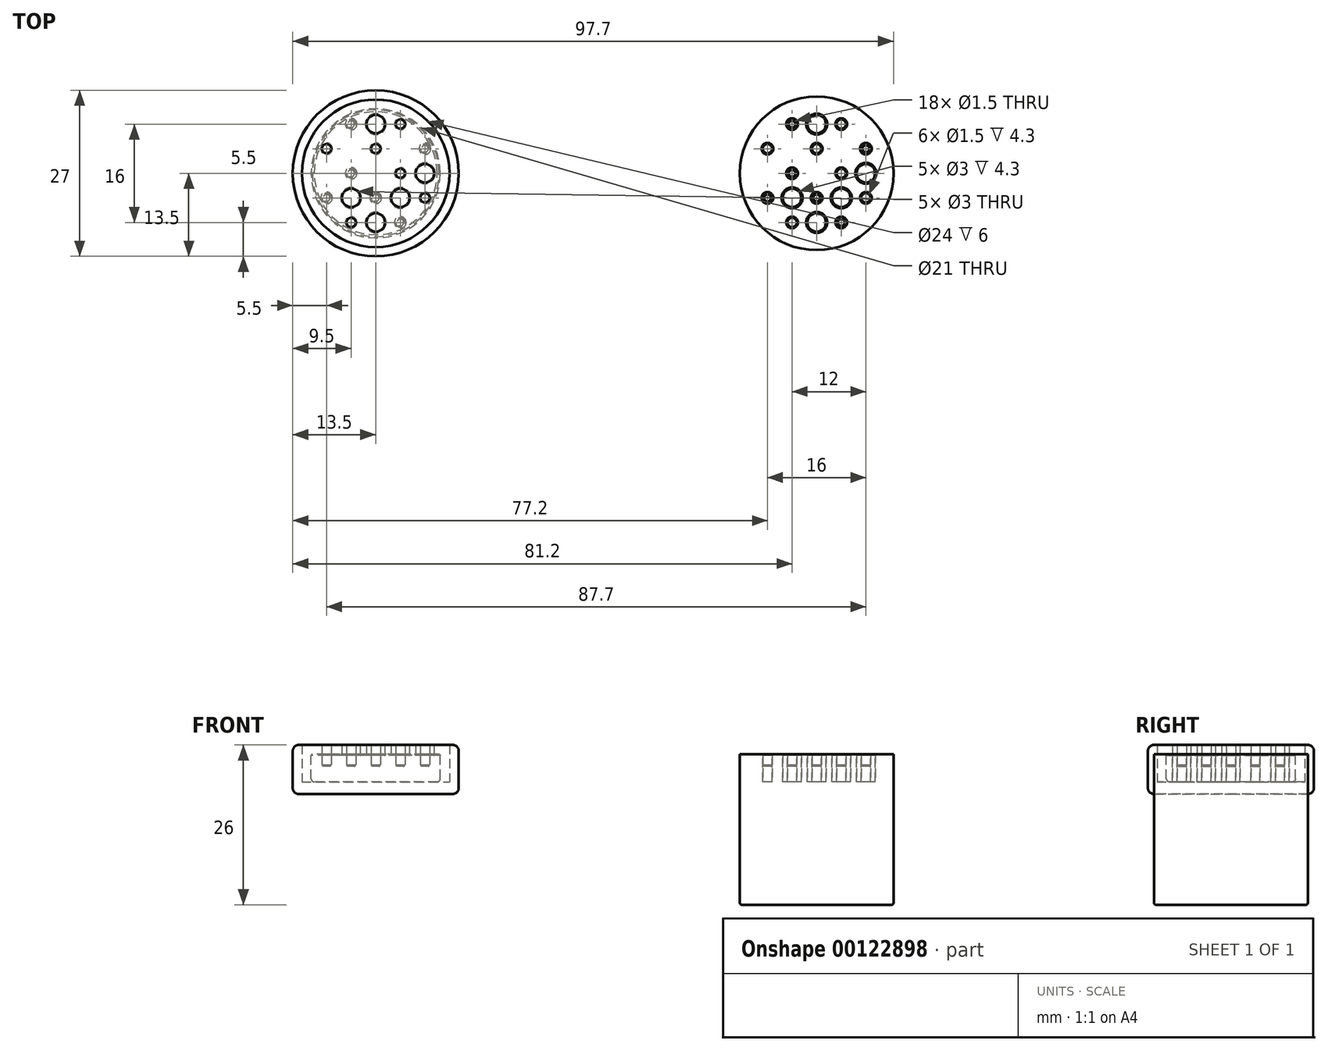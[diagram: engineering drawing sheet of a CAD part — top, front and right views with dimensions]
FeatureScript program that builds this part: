
annotation { "Feature Type Name" : "Feature", "Feature Type Description" : "" }
export const myFeature = defineFeature(function(context is Context, id is Id, definition is map)
    precondition{}
    {
        {
            var Q0;
            Q0=qCreatedBy(makeId("Top.planeOp"),FACE);
            var sketch = newSketch(context, id + "F0", { "sketchPlane" : qUnion([Q0])});
            skCircle(sketch, "E0", {"center": v(0, 0) * mm, "radius": 10.5 * mm});
            skCircle(sketch, "E1", {"center": v(0, 0) * mm, "radius": 1.5 * mm});
            skLineSegment(sketch, "E2", {"start": v(-10.5, 0) * mm, "end": v(10.5, 0) * mm, "construction": true});
            skCircle(sketch, "E3", {"center": v(-8, 0) * mm, "radius": 1.5 * mm});
            skLineSegment(sketch, "E4", {"start": v(0, 10.5) * mm, "end": v(0, -10.5) * mm, "construction": true});
            skCircle(sketch, "E5.MirrorC", {"center": v(8, 0) * mm, "radius": 1.5 * mm});
            skLineSegment(sketch, "E6", {"start": v(-7.42, 7.42) * mm, "end": v(7.42, -7.42) * mm, "construction": true});
            skCircle(sketch, "E7", {"center": v(-4, 4) * mm, "radius": 1.5 * mm});
            skLineSegment(sketch, "E8", {"start": v(-7.42, -7.42) * mm, "end": v(7.42, 7.42) * mm, "construction": true});
            skLineSegment(sketch, "E9", {"start": v(-10.25, -2.25) * mm, "end": v(2.25, 10.25) * mm, "construction": true});
            skLineSegment(sketch, "E10.MirrorCS", {"start": v(-2.25, -10.25) * mm, "end": v(10.25, 2.25) * mm, "construction": true});
            skLineSegment(sketch, "E11", {"start": v(-10.25, 2.25) * mm, "end": v(2.25, -10.25) * mm, "construction": true});
            skLineSegment(sketch, "E12.MirrorCS", {"start": v(-2.25, 10.25) * mm, "end": v(10.25, -2.25) * mm, "construction": true});
            skCircle(sketch, "E13.MirrorC", {"center": v(0, 8) * mm, "radius": 1.5 * mm});
            skCircle(sketch, "E14.MirrorC", {"center": v(0, -8) * mm, "radius": 1.5 * mm});
            skCircle(sketch, "E15.MirrorC", {"center": v(4, -4) * mm, "radius": 1.5 * mm});
            skCircle(sketch, "E16.MirrorC", {"center": v(4, 4) * mm, "radius": 1.5 * mm});
            skCircle(sketch, "E17.MirrorC", {"center": v(-4, -4) * mm, "radius": 1.5 * mm});
            skPoint(sketch, "E18", {"position": v(-4, 0) * mm});
            skPoint(sketch, "E19.MirrorP", {"position": v(0, 4) * mm});
            skPoint(sketch, "E20.MirrorP", {"position": v(4, 0) * mm});
            skPoint(sketch, "E21.MirrorP", {"position": v(0, -4) * mm});
            skPoint(sketch, "E22.MirrorP", {"position": v(-4, 8) * mm});
            skPoint(sketch, "E23.MirrorP", {"position": v(-8, 4) * mm});
            skPoint(sketch, "E24.MirrorP", {"position": v(8, -4) * mm});
            skPoint(sketch, "E25.MirrorP", {"position": v(4, -8) * mm});
            skPoint(sketch, "E26.MirrorP", {"position": v(4, 8) * mm});
            skPoint(sketch, "E27.MirrorP", {"position": v(8, 4) * mm});
            skPoint(sketch, "E28.MirrorP", {"position": v(-8, -4) * mm});
            skPoint(sketch, "E29.MirrorP", {"position": v(-4, -8) * mm});
            skCircle(sketch, "E30", {"center": v(-4, 8) * mm, "radius": 0.75 * mm});
            skCircle(sketch, "E31.MirrorC", {"center": v(-8, 4) * mm, "radius": 0.75 * mm});
            skCircle(sketch, "E32.MirrorC", {"center": v(0, 4) * mm, "radius": 0.75 * mm});
            skCircle(sketch, "E33.MirrorC", {"center": v(-4, 0) * mm, "radius": 0.75 * mm});
            skCircle(sketch, "E34.MirrorC", {"center": v(4, 8) * mm, "radius": 0.75 * mm});
            skCircle(sketch, "E35.MirrorC", {"center": v(8, 4) * mm, "radius": 0.75 * mm});
            skCircle(sketch, "E36.MirrorC", {"center": v(4, 0) * mm, "radius": 0.75 * mm});
            skCircle(sketch, "E37.MirrorC", {"center": v(-8, -4) * mm, "radius": 0.75 * mm});
            skCircle(sketch, "E38.MirrorC", {"center": v(-4, -8) * mm, "radius": 0.75 * mm});
            skCircle(sketch, "E39.MirrorC", {"center": v(4, -8) * mm, "radius": 0.75 * mm});
            skCircle(sketch, "E40.MirrorC", {"center": v(0, -4) * mm, "radius": 0.75 * mm});
            skCircle(sketch, "E41.MirrorC", {"center": v(8, -4) * mm, "radius": 0.75 * mm});
            skSolve(sketch);
        }
        {
            var Q0;
            Q0=makeQuery(id+"F0.imprint","IMPRINT",FACE,{"disambiguationData":[TD([[makeQuery(id+"F0.imprint","IMPRINT",EDGE,{"derivedFrom":sQuery(id+"F0.wireOp",EDGE,"E1")}),1.0]])]});
            var Q1;
            Q1=makeQuery(id+"F0.imprint","IMPRINT",FACE,{"disambiguationData":[TD([[makeQuery(id+"F0.imprint","IMPRINT",EDGE,{"derivedFrom":sQuery(id+"F0.wireOp",EDGE,"E3")}),1.0]])]});
            var Q2;
            Q2=makeQuery(id+"F0.imprint","IMPRINT",FACE,{"disambiguationData":[TD([[makeQuery(id+"F0.imprint","IMPRINT",EDGE,{"derivedFrom":sQuery(id+"F0.wireOp",EDGE,"E7")}),1.0]])]});
            var Q3;
            Q3=makeQuery(id+"F0.imprint","IMPRINT",FACE,{"disambiguationData":[TD([[makeQuery(id+"F0.imprint","IMPRINT",EDGE,{"derivedFrom":sQuery(id+"F0.wireOp",EDGE,"E13.MirrorC")}),-1.0]])]});
            var Q4;
            Q4=makeQuery(id+"F0.imprint","IMPRINT",FACE,{"disambiguationData":[TD([[makeQuery(id+"F0.imprint","IMPRINT",EDGE,{"derivedFrom":sQuery(id+"F0.wireOp",EDGE,"E5.MirrorC")}),1.0]])]});
            var Q5;
            Q5=makeQuery(id+"F0.imprint","IMPRINT",FACE,{"disambiguationData":[TD([[makeQuery(id+"F0.imprint","IMPRINT",EDGE,{"derivedFrom":sQuery(id+"F0.wireOp",EDGE,"E14.MirrorC")}),-1.0]])]});
            var Q6;
            Q6=makeQuery(id+"F0.imprint","IMPRINT",FACE,{"disambiguationData":[TD([[makeQuery(id+"F0.imprint","IMPRINT",EDGE,{"derivedFrom":sQuery(id+"F0.wireOp",EDGE,"E15.MirrorC")}),-1.0]])]});
            var Q7;
            Q7=makeQuery(id+"F0.imprint","IMPRINT",FACE,{"disambiguationData":[TD([[makeQuery(id+"F0.imprint","IMPRINT",EDGE,{"derivedFrom":sQuery(id+"F0.wireOp",EDGE,"E16.MirrorC")}),1.0]])]});
            var Q8;
            Q8=makeQuery(id+"F0.imprint","IMPRINT",FACE,{"disambiguationData":[TD([[makeQuery(id+"F0.imprint","IMPRINT",EDGE,{"derivedFrom":sQuery(id+"F0.wireOp",EDGE,"E17.MirrorC")}),-1.0]])]});
            var Q9;
            Q9=makeQuery(id+"F0.imprint","IMPRINT",FACE,{"disambiguationData":[TD([[makeQuery(id+"F0.imprint","IMPRINT",EDGE,{"derivedFrom":sQuery(id+"F0.wireOp",EDGE,"E0")}),1.0]])]});
            var Q10;
            Q10=makeQuery(id+"F0.imprint","IMPRINT",FACE,{"disambiguationData":[TD([[makeQuery(id+"F0.imprint","IMPRINT",EDGE,{"derivedFrom":sQuery(id+"F0.wireOp",EDGE,"E36.MirrorC")}),-1.0]])]});
            var Q11;
            Q11=makeQuery(id+"F0.imprint","IMPRINT",FACE,{"disambiguationData":[TD([[makeQuery(id+"F0.imprint","IMPRINT",EDGE,{"derivedFrom":sQuery(id+"F0.wireOp",EDGE,"E40.MirrorC")}),1.0]])]});
            var Q12;
            Q12=makeQuery(id+"F0.imprint","IMPRINT",FACE,{"disambiguationData":[TD([[makeQuery(id+"F0.imprint","IMPRINT",EDGE,{"derivedFrom":sQuery(id+"F0.wireOp",EDGE,"E41.MirrorC")}),-1.0]])]});
            var Q13;
            Q13=makeQuery(id+"F0.imprint","IMPRINT",FACE,{"disambiguationData":[TD([[makeQuery(id+"F0.imprint","IMPRINT",EDGE,{"derivedFrom":sQuery(id+"F0.wireOp",EDGE,"E34.MirrorC")}),-1.0]])]});
            var Q14;
            Q14=makeQuery(id+"F0.imprint","IMPRINT",FACE,{"disambiguationData":[TD([[makeQuery(id+"F0.imprint","IMPRINT",EDGE,{"derivedFrom":sQuery(id+"F0.wireOp",EDGE,"E35.MirrorC")}),1.0]])]});
            var Q15;
            Q15=makeQuery(id+"F0.imprint","IMPRINT",FACE,{"disambiguationData":[TD([[makeQuery(id+"F0.imprint","IMPRINT",EDGE,{"derivedFrom":sQuery(id+"F0.wireOp",EDGE,"E37.MirrorC")}),1.0]])]});
            var Q16;
            Q16=makeQuery(id+"F0.imprint","IMPRINT",FACE,{"disambiguationData":[TD([[makeQuery(id+"F0.imprint","IMPRINT",EDGE,{"derivedFrom":sQuery(id+"F0.wireOp",EDGE,"E30")}),1.0]])]});
            var Q17;
            Q17=makeQuery(id+"F0.imprint","IMPRINT",FACE,{"disambiguationData":[TD([[makeQuery(id+"F0.imprint","IMPRINT",EDGE,{"derivedFrom":sQuery(id+"F0.wireOp",EDGE,"E31.MirrorC")}),-1.0]])]});
            var Q18;
            Q18=makeQuery(id+"F0.imprint","IMPRINT",FACE,{"disambiguationData":[TD([[makeQuery(id+"F0.imprint","IMPRINT",EDGE,{"derivedFrom":sQuery(id+"F0.wireOp",EDGE,"E32.MirrorC")}),-1.0]])]});
            var Q19;
            Q19=makeQuery(id+"F0.imprint","IMPRINT",FACE,{"disambiguationData":[TD([[makeQuery(id+"F0.imprint","IMPRINT",EDGE,{"derivedFrom":sQuery(id+"F0.wireOp",EDGE,"E33.MirrorC")}),1.0]])]});
            var Q20;
            Q20=makeQuery(id+"F0.imprint","IMPRINT",FACE,{"disambiguationData":[TD([[makeQuery(id+"F0.imprint","IMPRINT",EDGE,{"derivedFrom":sQuery(id+"F0.wireOp",EDGE,"E38.MirrorC")}),-1.0]])]});
            var Q21;
            Q21=makeQuery(id+"F0.imprint","IMPRINT",FACE,{"disambiguationData":[TD([[makeQuery(id+"F0.imprint","IMPRINT",EDGE,{"derivedFrom":sQuery(id+"F0.wireOp",EDGE,"E39.MirrorC")}),1.0]])]});
            extrude(context, id + "F1", {"entities" : qUnion([Q0, Q1, Q2, Q3, Q4, Q5, Q6, Q7, Q8, Q9, Q10, Q11, Q12, Q13, Q14, Q15, Q16, Q17, Q18, Q19, Q20, Q21]), "oppositeDirection" : true, "depth" : 1.5 * mm});
        }
        {
            var Q0;
            Q0=makeQuery(id+"F0.imprint","IMPRINT",FACE,{"disambiguationData":[TD([[makeQuery(id+"F0.imprint","IMPRINT",EDGE,{"derivedFrom":sQuery(id+"F0.wireOp",EDGE,"E7")}),1.0]])]});
            var Q1;
            Q1=makeQuery(id+"F0.imprint","IMPRINT",FACE,{"disambiguationData":[TD([[makeQuery(id+"F0.imprint","IMPRINT",EDGE,{"derivedFrom":sQuery(id+"F0.wireOp",EDGE,"E13.MirrorC")}),-1.0]])]});
            var Q2;
            Q2=makeQuery(id+"F0.imprint","IMPRINT",FACE,{"disambiguationData":[TD([[makeQuery(id+"F0.imprint","IMPRINT",EDGE,{"derivedFrom":sQuery(id+"F0.wireOp",EDGE,"E16.MirrorC")}),1.0]])]});
            var Q3;
            Q3=makeQuery(id+"F0.imprint","IMPRINT",FACE,{"disambiguationData":[TD([[makeQuery(id+"F0.imprint","IMPRINT",EDGE,{"derivedFrom":sQuery(id+"F0.wireOp",EDGE,"E5.MirrorC")}),1.0]])]});
            var Q4;
            Q4=makeQuery(id+"F0.imprint","IMPRINT",FACE,{"disambiguationData":[TD([[makeQuery(id+"F0.imprint","IMPRINT",EDGE,{"derivedFrom":sQuery(id+"F0.wireOp",EDGE,"E15.MirrorC")}),-1.0]])]});
            var Q5;
            Q5=makeQuery(id+"F0.imprint","IMPRINT",FACE,{"disambiguationData":[TD([[makeQuery(id+"F0.imprint","IMPRINT",EDGE,{"derivedFrom":sQuery(id+"F0.wireOp",EDGE,"E1")}),1.0]])]});
            var Q6;
            Q6=makeQuery(id+"F0.imprint","IMPRINT",FACE,{"disambiguationData":[TD([[makeQuery(id+"F0.imprint","IMPRINT",EDGE,{"derivedFrom":sQuery(id+"F0.wireOp",EDGE,"E14.MirrorC")}),-1.0]])]});
            var Q7;
            Q7=makeQuery(id+"F0.imprint","IMPRINT",FACE,{"disambiguationData":[TD([[makeQuery(id+"F0.imprint","IMPRINT",EDGE,{"derivedFrom":sQuery(id+"F0.wireOp",EDGE,"E17.MirrorC")}),-1.0]])]});
            var Q8;
            Q8=makeQuery(id+"F0.imprint","IMPRINT",FACE,{"disambiguationData":[TD([[makeQuery(id+"F0.imprint","IMPRINT",EDGE,{"derivedFrom":sQuery(id+"F0.wireOp",EDGE,"E3")}),1.0]])]});
            extrude(context, id + "F2", {"entities" : qUnion([Q0, Q1, Q2, Q3, Q4, Q5, Q6, Q7, Q8]), "operationType" : NewBodyOperationType.ADD, "depth" : 3 * mm});
        }
        {
            var Q0;
            Q0=makeQuery(id+"F0.imprint","IMPRINT",FACE,{"disambiguationData":[TD([[makeQuery(id+"F0.imprint","IMPRINT",EDGE,{"derivedFrom":sQuery(id+"F0.wireOp",EDGE,"E30")}),1.0]])]});
            var Q1;
            Q1=makeQuery(id+"F0.imprint","IMPRINT",FACE,{"disambiguationData":[TD([[makeQuery(id+"F0.imprint","IMPRINT",EDGE,{"derivedFrom":sQuery(id+"F0.wireOp",EDGE,"E31.MirrorC")}),-1.0]])]});
            var Q2;
            Q2=makeQuery(id+"F0.imprint","IMPRINT",FACE,{"disambiguationData":[TD([[makeQuery(id+"F0.imprint","IMPRINT",EDGE,{"derivedFrom":sQuery(id+"F0.wireOp",EDGE,"E37.MirrorC")}),1.0]])]});
            var Q3;
            Q3=makeQuery(id+"F0.imprint","IMPRINT",FACE,{"disambiguationData":[TD([[makeQuery(id+"F0.imprint","IMPRINT",EDGE,{"derivedFrom":sQuery(id+"F0.wireOp",EDGE,"E33.MirrorC")}),1.0]])]});
            var Q4;
            Q4=makeQuery(id+"F0.imprint","IMPRINT",FACE,{"disambiguationData":[TD([[makeQuery(id+"F0.imprint","IMPRINT",EDGE,{"derivedFrom":sQuery(id+"F0.wireOp",EDGE,"E32.MirrorC")}),-1.0]])]});
            var Q5;
            Q5=makeQuery(id+"F0.imprint","IMPRINT",FACE,{"disambiguationData":[TD([[makeQuery(id+"F0.imprint","IMPRINT",EDGE,{"derivedFrom":sQuery(id+"F0.wireOp",EDGE,"E34.MirrorC")}),-1.0]])]});
            var Q6;
            Q6=makeQuery(id+"F0.imprint","IMPRINT",FACE,{"disambiguationData":[TD([[makeQuery(id+"F0.imprint","IMPRINT",EDGE,{"derivedFrom":sQuery(id+"F0.wireOp",EDGE,"E35.MirrorC")}),1.0]])]});
            var Q7;
            Q7=makeQuery(id+"F0.imprint","IMPRINT",FACE,{"disambiguationData":[TD([[makeQuery(id+"F0.imprint","IMPRINT",EDGE,{"derivedFrom":sQuery(id+"F0.wireOp",EDGE,"E36.MirrorC")}),-1.0]])]});
            var Q8;
            Q8=makeQuery(id+"F0.imprint","IMPRINT",FACE,{"disambiguationData":[TD([[makeQuery(id+"F0.imprint","IMPRINT",EDGE,{"derivedFrom":sQuery(id+"F0.wireOp",EDGE,"E40.MirrorC")}),1.0]])]});
            var Q9;
            Q9=makeQuery(id+"F0.imprint","IMPRINT",FACE,{"disambiguationData":[TD([[makeQuery(id+"F0.imprint","IMPRINT",EDGE,{"derivedFrom":sQuery(id+"F0.wireOp",EDGE,"E38.MirrorC")}),-1.0]])]});
            var Q10;
            Q10=makeQuery(id+"F0.imprint","IMPRINT",FACE,{"disambiguationData":[TD([[makeQuery(id+"F0.imprint","IMPRINT",EDGE,{"derivedFrom":sQuery(id+"F0.wireOp",EDGE,"E39.MirrorC")}),1.0]])]});
            var Q11;
            Q11=makeQuery(id+"F0.imprint","IMPRINT",FACE,{"disambiguationData":[TD([[makeQuery(id+"F0.imprint","IMPRINT",EDGE,{"derivedFrom":sQuery(id+"F0.wireOp",EDGE,"E41.MirrorC")}),-1.0]])]});
            extrude(context, id + "F3", {"entities" : qUnion([Q0, Q1, Q2, Q3, Q4, Q5, Q6, Q7, Q8, Q9, Q10, Q11]), "operationType" : NewBodyOperationType.ADD, "depth" : 1 * mm});
        }
        {
            var Q0;
            Q0=makeQuery(id+"F3.opExtrude","CAP_EDGE",EDGE,{"disambiguationData":[OSD([sQuery(id+"F0.wireOp",EDGE,"E37.MirrorC")])],"isStart":false});
            var Q1;
            Q1=makeQuery(id+"F3.opExtrude","CAP_EDGE",EDGE,{"disambiguationData":[OSD([sQuery(id+"F0.wireOp",EDGE,"E31.MirrorC")])],"isStart":false});
            var Q2;
            Q2=makeQuery(id+"F3.opExtrude","CAP_EDGE",EDGE,{"disambiguationData":[OSD([sQuery(id+"F0.wireOp",EDGE,"E30")])],"isStart":false});
            var Q3;
            Q3=makeQuery(id+"F3.opExtrude","CAP_EDGE",EDGE,{"disambiguationData":[OSD([sQuery(id+"F0.wireOp",EDGE,"E33.MirrorC")])],"isStart":false});
            var Q4;
            Q4=makeQuery(id+"F3.opExtrude","CAP_EDGE",EDGE,{"disambiguationData":[OSD([sQuery(id+"F0.wireOp",EDGE,"E32.MirrorC")])],"isStart":false});
            var Q5;
            Q5=makeQuery(id+"F3.opExtrude","CAP_EDGE",EDGE,{"disambiguationData":[OSD([sQuery(id+"F0.wireOp",EDGE,"E34.MirrorC")])],"isStart":false});
            var Q6;
            Q6=makeQuery(id+"F3.opExtrude","CAP_EDGE",EDGE,{"disambiguationData":[OSD([sQuery(id+"F0.wireOp",EDGE,"E35.MirrorC")])],"isStart":false});
            var Q7;
            Q7=makeQuery(id+"F3.opExtrude","CAP_EDGE",EDGE,{"disambiguationData":[OSD([sQuery(id+"F0.wireOp",EDGE,"E36.MirrorC")])],"isStart":false});
            var Q8;
            Q8=makeQuery(id+"F3.opExtrude","CAP_EDGE",EDGE,{"disambiguationData":[OSD([sQuery(id+"F0.wireOp",EDGE,"E40.MirrorC")])],"isStart":false});
            var Q9;
            Q9=makeQuery(id+"F3.opExtrude","CAP_FACE",FACE,{"disambiguationData":[OSD([sQuery(id+"F0.wireOp",EDGE,"E38.MirrorC")])],"isStart":false});
            var Q10;
            Q10=makeQuery(id+"F3.opExtrude","CAP_EDGE",EDGE,{"disambiguationData":[OSD([sQuery(id+"F0.wireOp",EDGE,"E39.MirrorC")])],"isStart":false});
            var Q11;
            Q11=makeQuery(id+"F3.opExtrude","CAP_EDGE",EDGE,{"disambiguationData":[OSD([sQuery(id+"F0.wireOp",EDGE,"E41.MirrorC")])],"isStart":false});
            var Q12;
            Q12=makeQuery(id+"F2.opExtrude","CAP_FACE",FACE,{"disambiguationData":[OSD([sQuery(id+"F0.wireOp",EDGE,"E3")])],"isStart":false});
            var Q13;
            Q13=makeQuery(id+"F2.opExtrude","CAP_FACE",FACE,{"disambiguationData":[OSD([sQuery(id+"F0.wireOp",EDGE,"E17.MirrorC")])],"isStart":false});
            var Q14;
            Q14=makeQuery(id+"F2.opExtrude","CAP_FACE",FACE,{"disambiguationData":[OSD([sQuery(id+"F0.wireOp",EDGE,"E14.MirrorC")])],"isStart":false});
            var Q15;
            Q15=makeQuery(id+"F2.opExtrude","CAP_FACE",FACE,{"disambiguationData":[OSD([sQuery(id+"F0.wireOp",EDGE,"E15.MirrorC")])],"isStart":false});
            var Q16;
            Q16=makeQuery(id+"F2.opExtrude","CAP_FACE",FACE,{"disambiguationData":[OSD([sQuery(id+"F0.wireOp",EDGE,"E1")])],"isStart":false});
            var Q17;
            Q17=makeQuery(id+"F2.opExtrude","CAP_FACE",FACE,{"disambiguationData":[OSD([sQuery(id+"F0.wireOp",EDGE,"E7")])],"isStart":false});
            var Q18;
            Q18=makeQuery(id+"F2.opExtrude","CAP_FACE",FACE,{"disambiguationData":[OSD([sQuery(id+"F0.wireOp",EDGE,"E13.MirrorC")])],"isStart":false});
            var Q19;
            Q19=makeQuery(id+"F2.opExtrude","CAP_FACE",FACE,{"disambiguationData":[OSD([sQuery(id+"F0.wireOp",EDGE,"E16.MirrorC")])],"isStart":false});
            var Q20;
            Q20=makeQuery(id+"F2.opExtrude","CAP_FACE",FACE,{"disambiguationData":[OSD([sQuery(id+"F0.wireOp",EDGE,"E5.MirrorC")])],"isStart":false});
            var Q21;
            Q21=makeQuery(id+"F1.opExtrude","CAP_EDGE",EDGE,{"disambiguationData":[OSD([sQuery(id+"F0.wireOp",EDGE,"E0")])],"isStart":true});
            chamfer(context, id + "F4", {"entities" : qUnion([Q0, Q1, Q2, Q3, Q4, Q5, Q6, Q7, Q8, Q9, Q10, Q11, Q12, Q13, Q14, Q15, Q16, Q17, Q18, Q19, Q20, Q21]), "width" : 0.2 * mm, "tangentPropagation" : true});
        }
        {
            var Q0;
            Q0=makeQuery(id+"F1.opExtrude","CAP_EDGE",EDGE,{"disambiguationData":[OSD([sQuery(id+"F0.wireOp",EDGE,"E0")])],"isStart":false});
            fillet(context, id + "F5", {"entities" : qUnion([Q0]), "radius" : 0.5 * mm, "tangentPropagation" : true, "allowEdgeOverflow" : false});
        }
        {
            var Q0;
            Q0=makeQuery(id+"F1.opExtrude","CAP_FACE",FACE,{"disambiguationData":[OSD([sQuery(id+"F0.wireOp",EDGE,"E0")])],"isStart":false});
            var sketch = newSketch(context, id + "F6", { "sketchPlane" : qUnion([Q0])});
            skCircle(sketch, "E42", {"center": v(0, 0) * mm, "radius": 12 * mm});
            skSolve(sketch);
        }
        {
            var Q0;
            Q0=makeQuery(id+"F1.opExtrude","SWEPT_BODY",BODY,{"disambiguationData":[OSD([sQuery(id+"F0.wireOp",EDGE,"E0")])]});
            transform(context, id + "F7", {"entities" : qUnion([Q0]), "transformType" : TransformType.TRANSLATION_3D, "dx" : 71.7 * mm, "dy" : 0 * mm, "dz" : 0 * mm, "makeCopy" : true});
        }
        {
            var Q0;
            Q0=makeQuery(id+"F6.imprint","IMPRINT",FACE,{"disambiguationData":[TD([[makeQuery(id+"F6.imprint","IMPRINT",EDGE,{"derivedFrom":makeQuery(id+"F1.opExtrude","CAP_EDGE",EDGE,{"disambiguationData":[OSD([sQuery(id+"F0.wireOp",EDGE,"E0")])],"isStart":false})}),-1.0]])]});
            var Q1;
            Q1=makeQuery(id+"F6.imprint","IMPRINT",FACE,{"disambiguationData":[TD([[makeQuery(id+"F6.imprint","IMPRINT",EDGE,{"derivedFrom":sQuery(id+"F6.wireOp",EDGE,"E42")}),1.0]])]});
            var Q2;
            {var subQ0=sQuery(id+"F0.wireOp",EDGE,"E0");Q2=makeQuery(id+"F6.imprint","IMPRINT",FACE,{"disambiguationData":[TD([[makeQuery(id+"F6.imprint","IMPRINT",EDGE,{"derivedFrom":makeQuery(id+"F5.opFillet","BLEND_EDGE",EDGE,{"blendedFrom":[makeQuery(id+"F1.opExtrude","CAP_EDGE",EDGE,{"disambiguationData":[OSD([subQ0])],"isStart":false}),makeQuery(id+"F1.opExtrude","CAP_FACE",FACE,{"disambiguationData":[OSD([subQ0])],"isStart":false})],"blendedInto":[makeQuery(id+"F1.opExtrude","CAP_FACE",FACE,{"disambiguationData":[OSD([subQ0])],"isStart":false})]})}),1.0]])]});}
            var Q3;
            Q3=makeQuery(id+"F2.opExtrude","CAP_FACE",FACE,{"disambiguationData":[OSD([sQuery(id+"F0.wireOp",EDGE,"E14.MirrorC")])],"isStart":false});
            extrude(context, id + "F8", {"entities" : qUnion([Q0, Q1, Q2]), "oppositeDirection" : true, "endBoundEntityFace" : qUnion([Q3]), "depth" : 6 * mm});
        }
        {
            var Q0;
            Q0=makeQuery(id+"F1.opExtrude","SWEPT_BODY",BODY,{"disambiguationData":[OSD([sQuery(id+"F0.wireOp",EDGE,"E0")])]});
            var Q1;
            Q1=makeQuery(id+"F8.opExtrude","SWEPT_BODY",BODY,{"disambiguationData":[OSD([sQuery(id+"F6.wireOp",EDGE,"E42")])]});
            booleanBodies(context, id + "F9", {"operationType" : BooleanOperationType.SUBTRACTION, "tools" : qUnion([Q0]), "targets" : qUnion([Q1])});
        }
        {
            var Q0;
            Q0=makeQuery(id+"F8.opExtrude","CAP_FACE",FACE,{"disambiguationData":[OSD([sQuery(id+"F6.wireOp",EDGE,"E42")])],"isStart":true});
            cPlane(context, id + "F10", {"entities" : qUnion([Q0]), "cplaneType" : CPlaneType.OFFSET, "offset" : 2 * mm, "width" : 150 * mm, "height" : 150 * mm});
        }
        {
            var Q0;
            Q0=qCreatedBy(id+"F10.planeOp",FACE);
            var sketch = newSketch(context, id + "F11", { "sketchPlane" : qUnion([Q0])});
            skCircle(sketch, "E43", {"center": v(0, 0) * mm, "radius": 13.5 * mm});
            skSolve(sketch);
        }
        {
            var Q0;
            Q0=makeQuery(id+"F11.imprint","IMPRINT",FACE,{"disambiguationData":[TD([[makeQuery(id+"F11.imprint","IMPRINT",EDGE,{"derivedFrom":sQuery(id+"F11.wireOp",EDGE,"E43")}),1.0]])]});
            var Q1;
            Q1=makeQuery(id+"F8.opExtrude","CAP_FACE",FACE,{"disambiguationData":[OSD([sQuery(id+"F6.wireOp",EDGE,"E42")])],"isStart":false});
            extrude(context, id + "F12", {"entities" : qUnion([Q0]), "endBound" : BoundingType.UP_TO_SURFACE, "oppositeDirection" : true, "endBoundEntityFace" : qUnion([Q1]), "depth" : 25 * mm});
        }
        {
            var Q0;
            Q0=makeQuery(id+"F8.opExtrude","SWEPT_BODY",BODY,{"disambiguationData":[OSD([sQuery(id+"F6.wireOp",EDGE,"E42")])]});
            var Q1;
            Q1=makeQuery(id+"F12.opExtrude","SWEPT_BODY",BODY,{"disambiguationData":[OSD([sQuery(id+"F11.wireOp",EDGE,"E43")])]});
            booleanBodies(context, id + "F13", {"operationType" : BooleanOperationType.SUBTRACTION, "tools" : qUnion([Q0]), "targets" : qUnion([Q1]), "keepTools" : true});
        }
        {
            var Q0;
            Q0=makeQuery(id+"F12.opExtrude","TWEAK_EDGE",EDGE,{"derivedFrom":[makeQuery(id+"F8.opExtrude","CAP_FACE",FACE,{"disambiguationData":[OSD([sQuery(id+"F6.wireOp",EDGE,"E42")])],"isStart":false}),makeQuery(id+"F11.imprint","IMPRINT",EDGE,{"derivedFrom":sQuery(id+"F11.wireOp",EDGE,"E43")})]});
            var Q1;
            Q1=makeQuery(id+"F12.opExtrude","SWEPT_FACE",FACE,{"disambiguationData":[OSD([sQuery(id+"F11.wireOp",EDGE,"E43")])]});
            fillet(context, id + "F14", {"entities" : qUnion([Q0, Q1]), "radius" : 1 * mm, "tangentPropagation" : true, "allowEdgeOverflow" : false});
        }
        {
            var Q0;
            Q0=makeQuery(id+"F7.opPattern","COPY",FACE,{"derivedFrom":makeQuery(id+"F1.opExtrude","CAP_FACE",FACE,{"disambiguationData":[OSD([sQuery(id+"F0.wireOp",EDGE,"E0")])],"isStart":false}),"instanceName":"1"});
            var sketch = newSketch(context, id + "F15", { "sketchPlane" : qUnion([Q0])});
            skCircle(sketch, "E44", {"center": v(71.7, 0) * mm, "radius": 12.5 * mm});
            skSolve(sketch);
        }
        {
            var Q0;
            Q0 = qSketchRegion(id + "F15", true);
            extrude(context, id + "F16", {"entities" : qUnion([Q0]), "depth" : 20 * mm});
        }
        {
            var Q0;
            Q0=makeQuery(id+"F15.imprint","IMPRINT",FACE,{"disambiguationData":[TD([[makeQuery(id+"F15.imprint","IMPRINT",EDGE,{"derivedFrom":sQuery(id+"F15.wireOp",EDGE,"E44")}),1.0]])]});
            var Q1;
            Q1=makeQuery(id+"F7.opPattern","COPY",FACE,{"derivedFrom":makeQuery(id+"F2.opExtrude","CAP_FACE",FACE,{"disambiguationData":[OSD([sQuery(id+"F0.wireOp",EDGE,"E13.MirrorC")])],"isStart":false}),"instanceName":"1"});
            extrude(context, id + "F17", {"entities" : qUnion([Q0]), "operationType" : NewBodyOperationType.ADD, "endBound" : BoundingType.UP_TO_SURFACE, "oppositeDirection" : true, "endBoundEntityFace" : qUnion([Q1]), "depth" : 25 * mm});
        }
        {
            var Q0;
            Q0=makeQuery(id+"F16.opExtrude","CAP_FACE",FACE,{"disambiguationData":[OSD([sQuery(id+"F15.wireOp",EDGE,"E44")])],"isStart":true});
            var Q1;
            Q1=makeQuery(id+"F17.opExtrude","CAP_FACE",FACE,{"disambiguationData":[OSD([sQuery(id+"F0.wireOp",EDGE,"E13.MirrorC")])],"isStart":false});
            extrude(context, id + "F18", {"entities" : qUnion([Q0]), "endBound" : BoundingType.UP_TO_SURFACE, "endBoundEntityFace" : qUnion([Q1]), "depth" : 25 * mm});
        }
        {
            var Q0;
            Q0=makeQuery(id+"F7.opPattern","COPY",BODY,{"derivedFrom":makeQuery(id+"F1.opExtrude","SWEPT_BODY",BODY,{"disambiguationData":[OSD([sQuery(id+"F0.wireOp",EDGE,"E0")])]}),"instanceName":"1"});
            var Q1;
            Q1=makeQuery(id+"F18.opExtrude","SWEPT_BODY",BODY,{"disambiguationData":[OSD([sQuery(id+"F15.wireOp",EDGE,"E44")])]});
            booleanBodies(context, id + "F19", {"operationType" : BooleanOperationType.SUBTRACTION, "tools" : qUnion([Q0]), "targets" : qUnion([Q1]), "keepTools" : true});
        }
        {
            var Q0;
            Q0=makeQuery(id+"F17.opExtrude","TWEAK_EDGE",EDGE,{"derivedFrom":[makeQuery(id+"F7.opPattern","COPY",FACE,{"derivedFrom":makeQuery(id+"F2.opExtrude","CAP_FACE",FACE,{"disambiguationData":[OSD([sQuery(id+"F0.wireOp",EDGE,"E13.MirrorC")])],"isStart":false}),"instanceName":"1"}),makeQuery(id+"F15.imprint","IMPRINT",EDGE,{"derivedFrom":sQuery(id+"F15.wireOp",EDGE,"E44")})]});
            var Q1;
            Q1=makeQuery(id+"F16.opExtrude","CAP_EDGE",EDGE,{"disambiguationData":[OSD([sQuery(id+"F15.wireOp",EDGE,"E44")])],"isStart":false});
            fillet(context, id + "F20", {"entities" : qUnion([Q0, Q1]), "radius" : 0.3 * mm, "tangentPropagation" : true, "allowEdgeOverflow" : false});
        }
    });
